# Revit family: Bernhardt_Design-Tables-Multipurpose-Intersection_mobile
name_source: partatom
category: Furniture
units: mm (PartAtom-declared; Revit-internal decimal feet)

## family parameters
Always vertical = Yes
Cut with Voids When Loaded = No
OmniClass Number = 23.40.20.00
OmniClass Title = General Furniture and Specialties
Room Calculation Point = No
Shared = No
Work Plane-Based = No

## types (65) — shared parameters
Default Elevation = 0.000"
Manufacturer = Bernhardt Design
Model = Intersection
Modesty Position = 3.720"
URL = http://www.bernhardtdesign.com

## per-type parameters (varying)
| type | Catalog | Modesty Length Half | Modesty Panel Visibility | Rail Length | Rail Length Half | Rail Width Half | SKU | Table Length | Table Length Half | Table Width | Table Width Half |
| Intersection - MAA - 36x36 mobile | INS-MAA | 13.125" | No | 35.024" | 17.512" | 17.512" | INS-MAA | 36.000" | 18.000" | 36.000" | 18.000" |
| Intersection - MBB - 42x42 mobile | INS-MBB | 16.125" | No | 41.024" | 20.512" | 20.512" | INS-MBB | 42.000" | 21.000" | 42.000" | 21.000" |
| Intersection - MCC - 48x48 mobile | INS-MCC | 19.125" | No | 47.024" | 23.512" | 23.512" | INS-MCC | 48.000" | 24.000" | 48.000" | 24.000" |
| Intersection - MDD - 54x54 mobile w/ modesty | INS-MDD | 22.125" | Yes | 53.024" | 26.512" | 26.512" | INS-MDD | 54.000" | 27.000" | 54.000" | 27.000" |
| Intersection - MDD - 54x54 mobile | INS-MDD | 22.125" | No | 53.024" | 26.512" | 26.512" | INS-MDD | 54.000" | 27.000" | 54.000" | 27.000" |
| Intersection - MVC - 48x24 mobile | INS-MVC | 19.125" | No | 47.024" | 23.512" | 11.512" | INS-MVC | 48.000" | 24.000" | 24.000" | 12.000" |
| Intersection - MVD - 54x24 mobile | INS-MVD | 22.125" | No | 53.024" | 26.512" | 11.512" | INS-MVD | 54.000" | 27.000" | 24.000" | 12.000" |
| Intersection - MVD - 54x24 mobile w/ modesty | INS-MVD | 22.125" | Yes | 53.024" | 26.512" | 11.512" | INS-MVD | 54.000" | 27.000" | 24.000" | 12.000" |
| Intersection - MVE - 60x24 mobile | INS-MVE | 25.125" | No | 59.024" | 29.512" | 11.512" | INS-MVE | 60.000" | 30.000" | 24.000" | 12.000" |
| Intersection - MVE - 60x24 mobile w/ modesty | INS-MVE | 25.125" | Yes | 59.024" | 29.512" | 11.512" | INS-MVE | 60.000" | 30.000" | 24.000" | 12.000" |
| Intersection - MVF - 66x24 mobile | INS-MVF | 28.125" | No | 65.024" | 32.512" | 11.512" | INS-MVF | 66.000" | 33.000" | 24.000" | 12.000" |
| Intersection - MVF - 66x24 mobile w/ modesty | INS-MVF | 28.125" | Yes | 65.024" | 32.512" | 11.512" | INS-MVF | 66.000" | 33.000" | 24.000" | 12.000" |
| Intersection - MVG - 72x24 mobile | INS-MVG | 31.125" | No | 71.024" | 35.512" | 11.512" | INS-MVG | 72.000" | 36.000" | 24.000" | 12.000" |
| Intersection - MVG - 72x24 mobile w/ modesty | INS-MVG | 31.125" | Yes | 71.024" | 35.512" | 11.512" | INS-MVG | 72.000" | 36.000" | 24.000" | 12.000" |
| Intersection - MVH - 78x24 mobile | INS-MVH | 34.125" | No | 77.024" | 38.512" | 11.512" | INS-MVH | 78.000" | 39.000" | 24.000" | 12.000" |
| Intersection - MVH - 78x24 mobile w/ modesty | INS-MVH | 34.125" | Yes | 77.024" | 38.512" | 11.512" | INS-MVH | 78.000" | 39.000" | 24.000" | 12.000" |
| Intersection - MVI - 84x24 mobile | INS-MVI | 37.125" | No | 83.024" | 41.512" | 11.512" | INS-MVI | 84.000" | 42.000" | 24.000" | 12.000" |
| Intersection - MVI - 84x24 mobile w/ modesty | INS-MVI | 37.125" | Yes | 83.024" | 41.512" | 11.512" | INS-MVI | 84.000" | 42.000" | 24.000" | 12.000" |
| Intersection - MVJ - 90x24 mobile | INS-MVJ | 40.125" | No | 89.024" | 44.512" | 11.512" | INS-MVJ | 90.000" | 45.000" | 24.000" | 12.000" |
| Intersection - MOD - 54x30 mobile | INS-MOD | 22.125" | No | 53.024" | 26.512" | 14.512" | INS-MOD | 54.000" | 27.000" | 30.000" | 15.000" |
| Intersection - MOD - 54x30 mobile w/ modesty | INS-MOD | 22.125" | Yes | 53.024" | 26.512" | 14.512" | INS-MOD | 54.000" | 27.000" | 30.000" | 15.000" |
| Intersection - MOE - 60x30 mobile | INS-MOE | 25.125" | No | 59.024" | 29.512" | 14.512" | INS-MOE | 60.000" | 30.000" | 30.000" | 15.000" |
| Intersection - MOE - 60x30 mobile w/ modesty | INS-MOE | 25.125" | Yes | 59.024" | 29.512" | 14.512" | INS-MOE | 60.000" | 30.000" | 30.000" | 15.000" |
| Intersection - MOF - 66x30 mobile | INS-MOF | 28.125" | No | 65.024" | 32.512" | 14.512" | INS-MOF | 66.000" | 33.000" | 30.000" | 15.000" |
| Intersection - MOF - 66x30 mobile w/ modesty | INS-MOF | 28.125" | Yes | 65.024" | 32.512" | 14.512" | INS-MOF | 66.000" | 33.000" | 30.000" | 15.000" |
| Intersection - MOG - 72x30 mobile | INS-MOG | 31.125" | No | 71.024" | 35.512" | 14.512" | INS-MOG | 72.000" | 36.000" | 30.000" | 15.000" |
| Intersection - MOG - 72x30 mobile w/ modesty | INS-MOG | 31.125" | Yes | 71.024" | 35.512" | 14.512" | INS-MOG | 72.000" | 36.000" | 30.000" | 15.000" |
| Intersection - MOH - 78x30 mobile | INS-MOH | 34.125" | No | 77.024" | 38.512" | 14.512" | INS-MOH | 78.000" | 39.000" | 30.000" | 15.000" |
| Intersection - MOH - 78x30 mobile w/ modesty | INS-MOH | 34.125" | Yes | 77.024" | 38.512" | 14.512" | INS-MOH | 78.000" | 39.000" | 30.000" | 15.000" |
| Intersection - MOI - 84x30 mobile | INS-MOI | 37.125" | No | 83.024" | 41.512" | 14.512" | INS-MOI | 84.000" | 42.000" | 30.000" | 15.000" |
| Intersection - MOI - 84x30 mobile w/ modesty | INS-MOI | 37.125" | Yes | 83.024" | 41.512" | 14.512" | INS-MOI | 84.000" | 42.000" | 30.000" | 15.000" |
| Intersection - MOJ - 90x30 mobile | INS-MOJ | 40.125" | No | 89.024" | 44.512" | 14.512" | INS-MOJ | 90.000" | 45.000" | 30.000" | 15.000" |
| Intersection - MAE - 60x36 mobile | INS-MAE | 25.125" | No | 59.024" | 29.512" | 17.512" | INS-MAE | 60.000" | 30.000" | 36.000" | 18.000" |
| Intersection - MAE - 60x36 mobile w/ modesty | INS-MAE | 25.125" | Yes | 59.024" | 29.512" | 17.512" | INS-MAE | 60.000" | 30.000" | 36.000" | 18.000" |
| Intersection - MAF - 66x36 mobile | INS-MAF | 28.125" | No | 65.024" | 32.512" | 17.512" | INS-MAF | 66.000" | 33.000" | 36.000" | 18.000" |
| Intersection - MAF - 66x36 mobile w/ modesty | INS-MAF | 28.125" | Yes | 65.024" | 32.512" | 17.512" | INS-MAF | 66.000" | 33.000" | 36.000" | 18.000" |
| Intersection - MAG - 72x36 mobile | INS-MAG | 31.125" | No | 71.024" | 35.512" | 17.512" | INS-MAG | 72.000" | 36.000" | 36.000" | 18.000" |
| Intersection - MAG - 72x36 mobile w/ modesty | INS-MAG | 31.125" | Yes | 71.024" | 35.512" | 17.512" | INS-MAG | 72.000" | 36.000" | 36.000" | 18.000" |
| Intersection - MAH - 78x36 mobile | INS-MAH | 34.125" | No | 77.024" | 38.512" | 17.512" | INS-MAH | 78.000" | 39.000" | 36.000" | 18.000" |
| Intersection - MAH - 78x36 mobile w/ modesty | INS-MAH | 34.125" | Yes | 77.024" | 38.512" | 17.512" | INS-MAH | 78.000" | 39.000" | 36.000" | 18.000" |
| Intersection - MAI - 84x36 mobile | INS-MAI | 37.125" | No | 83.024" | 41.512" | 17.512" | INS-MAI | 84.000" | 42.000" | 36.000" | 18.000" |
| Intersection - MAI - 84x36 mobile w/ modesty | INS-MAI | 37.125" | Yes | 83.024" | 41.512" | 17.512" | INS-MAI | 84.000" | 42.000" | 36.000" | 18.000" |
| Intersection - MAJ -90x36 mobile | INS-MAJ | 40.125" | No | 89.024" | 44.512" | 17.512" | INS-MAJ | 90.000" | 45.000" | 36.000" | 18.000" |
| Intersection - MBE - 60x42 mobile | INS-MBE | 25.125" | No | 59.024" | 29.512" | 20.512" | INS-MBE | 60.000" | 30.000" | 42.000" | 21.000" |
| Intersection - MBE - 60x42 mobile w/ modesty | INS-MBE | 25.125" | Yes | 59.024" | 29.512" | 20.512" | INS-MBE | 60.000" | 30.000" | 42.000" | 21.000" |
| Intersection - MBF - 66x42 mobile | INS-MBF | 28.125" | No | 65.024" | 32.512" | 20.512" | INS-MBF | 66.000" | 33.000" | 42.000" | 21.000" |
| Intersection - MBF - 66x42 mobile w/ modesty | INS-MBF | 28.125" | Yes | 65.024" | 32.512" | 20.512" | INS-MBF | 66.000" | 33.000" | 42.000" | 21.000" |
| Intersection - MBG - 72x42 mobile | INS-MBG | 31.125" | No | 71.024" | 35.512" | 20.512" | INS-MBG | 72.000" | 36.000" | 42.000" | 21.000" |
| Intersection - MBG - 72x42 mobile w/ modesty | INS-MBG | 31.125" | Yes | 71.024" | 35.512" | 20.512" | INS-MBG | 72.000" | 36.000" | 42.000" | 21.000" |
| Intersection - MBH - 78x42 mobile | INS-MBH | 34.125" | No | 77.024" | 38.512" | 20.512" | INS-MBH | 78.000" | 39.000" | 42.000" | 21.000" |
| Intersection - MBH - 78x42 mobile w/ modesty | INS-MBH | 34.125" | Yes | 77.024" | 38.512" | 20.512" | INS-MBH | 78.000" | 39.000" | 42.000" | 21.000" |
| Intersection - MBI - 84x42 mobile | INS-MBI | 37.125" | No | 83.024" | 41.512" | 20.512" | INS-MBI | 84.000" | 42.000" | 42.000" | 21.000" |
| Intersection - MBI - 84x42 mobile w/ modesty | INS-MBI | 37.125" | Yes | 83.024" | 41.512" | 20.512" | INS-MBI | 84.000" | 42.000" | 42.000" | 21.000" |
| Intersection - MBJ - 90x42 mobile | INS-MBJ | 40.125" | No | 89.024" | 44.512" | 20.512" | INS-MBJ | 90.000" | 45.000" | 42.000" | 21.000" |
| Intersection - MCE - 60x48 mobile | INS-MCE | 25.125" | No | 59.024" | 29.512" | 23.512" | INS-MCE | 60.000" | 30.000" | 48.000" | 24.000" |
| Intersection - MCE - 60x48 mobile w/ modesty | INS-MCE | 25.125" | Yes | 59.024" | 29.512" | 23.512" | INS-MCE | 60.000" | 30.000" | 48.000" | 24.000" |
| Intersection - MCF - 66x48 mobile | INS-MCF | 28.125" | No | 65.024" | 32.512" | 23.512" | INS-MCF | 66.000" | 33.000" | 48.000" | 24.000" |
| Intersection - MCF - 66x48 mobile w/ modesty | INS-MCF | 28.125" | Yes | 65.024" | 32.512" | 23.512" | INS-MCF | 66.000" | 33.000" | 48.000" | 24.000" |
| Intersection - MCG - 72x48 mobile | INS-MCG | 31.125" | No | 71.024" | 35.512" | 23.512" | INS-MCG | 72.000" | 36.000" | 48.000" | 24.000" |
| Intersection - MCG - 72x48 mobile w/ modesty | INS-MCG | 31.125" | Yes | 71.024" | 35.512" | 23.512" | INS-MCG | 72.000" | 36.000" | 48.000" | 24.000" |
| Intersection - MCH - 78x48 mobile | INS-MCH | 34.125" | No | 77.024" | 38.512" | 23.512" | INS-MCH | 78.000" | 39.000" | 48.000" | 24.000" |
| Intersection - MCH - 78x48 mobile w/ modesty | INS-MCH | 34.125" | Yes | 77.024" | 38.512" | 23.512" | INS-MCH | 78.000" | 39.000" | 48.000" | 24.000" |
| Intersection - MCI - 84x48 mobile | INS-MCI | 37.125" | No | 83.024" | 41.512" | 23.512" | INS-MCI | 84.000" | 42.000" | 48.000" | 24.000" |
| Intersection - MCI - 84x48 mobile w/ modesty | INS-MCI | 37.125" | Yes | 83.024" | 41.512" | 23.512" | INS-MCI | 84.000" | 42.000" | 48.000" | 24.000" |
| Intersection - MCJ - 90x48 mobile | INS-MCJ | 40.125" | No | 89.024" | 44.512" | 23.512" | INS-MCJ | 90.000" | 45.000" | 48.000" | 24.000" |

## geometry (parser evidence)
native form markers: Sweep x5
no freeform markers — native parametric forms only
